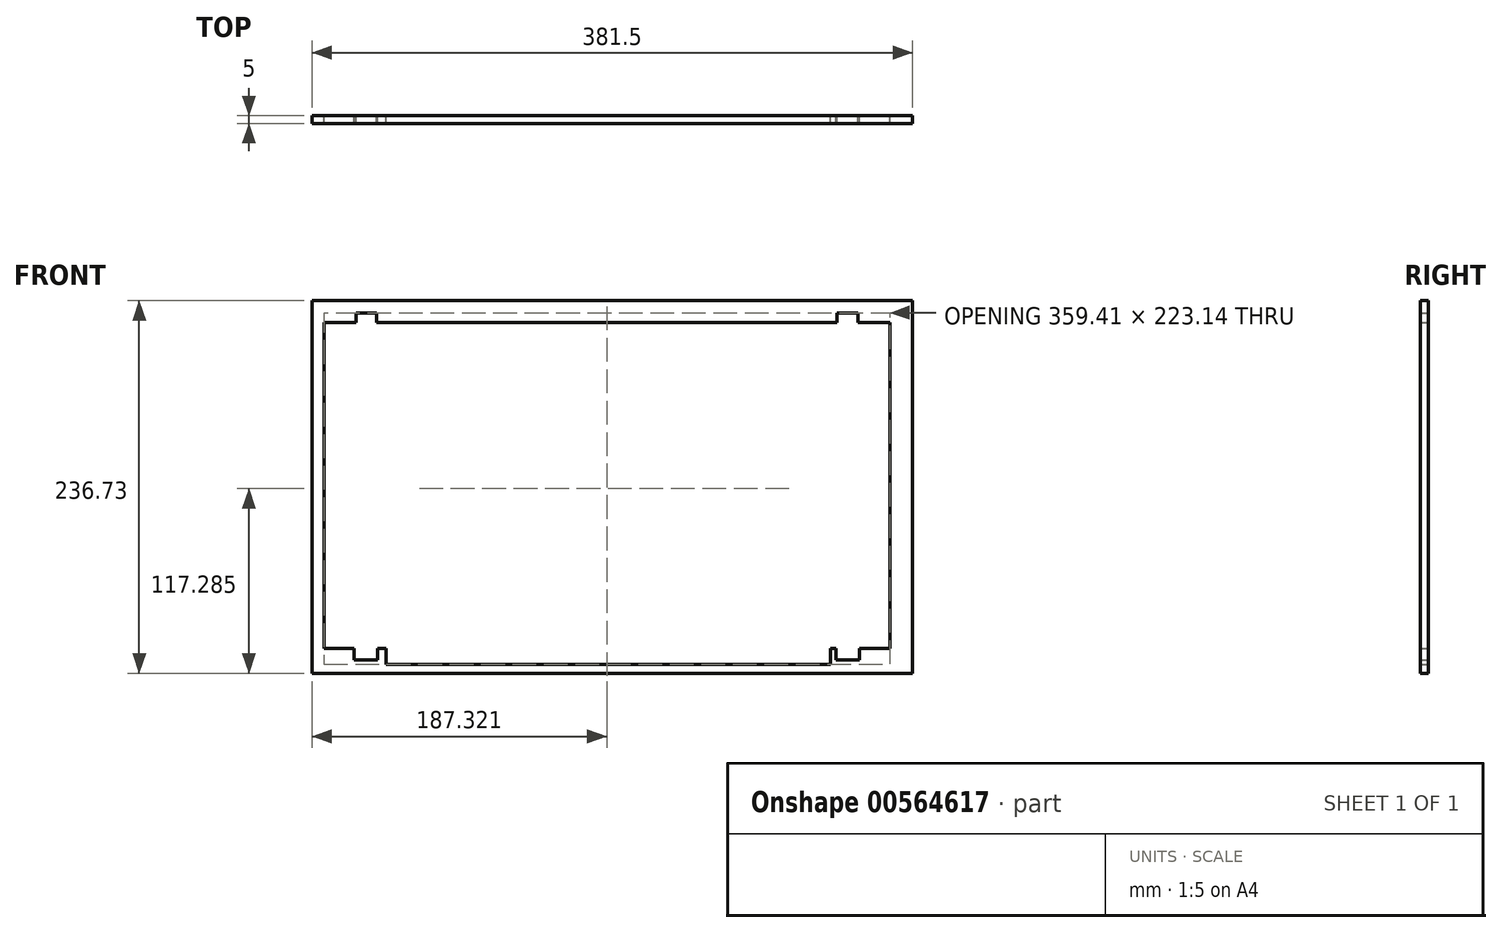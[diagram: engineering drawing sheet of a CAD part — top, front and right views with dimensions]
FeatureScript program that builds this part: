
annotation { "Feature Type Name" : "Feature", "Feature Type Description" : "" }
export const myFeature = defineFeature(function(context is Context, id is Id, definition is map)
    precondition{}
    {
        {
            var Q0;
            Q0=qCreatedBy(makeId("Front.planeOp"),FACE);
            var sketch = newSketch(context, id + "F0", { "sketchPlane" : qUnion([Q0])});
            skLineSegment(sketch, "E0.bottom", {"start": v(-180.8, 26.26) * mm, "end": v(-160.47, 26.26) * mm});
            skLineSegment(sketch, "E0.left", {"start": v(-180.8, 26.26) * mm, "end": v(-180.8, -180.75) * mm});
            skLineSegment(sketch, "E0.right", {"start": v(178.62, 26.26) * mm, "end": v(178.62, -180.75) * mm});
            skLineSegment(sketch, "E1", {"start": v(178.62, 26.26) * mm, "end": v(178.62, 32.36) * mm, "construction": true});
            skLineSegment(sketch, "E2", {"start": v(178.62, 32.36) * mm, "end": v(158.3, 32.36) * mm, "construction": true});
            skLineSegment(sketch, "E3", {"start": v(158.3, 32.36) * mm, "end": v(158.3, 26.26) * mm});
            skLineSegment(sketch, "E4", {"start": v(158.3, 32.36) * mm, "end": v(145.09, 32.36) * mm});
            skLineSegment(sketch, "E5", {"start": v(145.09, 32.36) * mm, "end": v(145.09, 26.26) * mm});
            skLineSegment(sketch, "E6", {"start": v(178.62, -180.75) * mm, "end": v(178.62, -187.99) * mm, "construction": true});
            skLineSegment(sketch, "E7", {"start": v(178.62, -187.99) * mm, "end": v(159.52, -187.99) * mm, "construction": true});
            skLineSegment(sketch, "E8", {"start": v(159.52, -187.99) * mm, "end": v(159.52, -180.75) * mm});
            skLineSegment(sketch, "E9", {"start": v(159.52, -187.99) * mm, "end": v(144.4, -187.99) * mm});
            skLineSegment(sketch, "E10", {"start": v(144.4, -187.99) * mm, "end": v(144.4, -180.75) * mm});
            skLineSegment(sketch, "E11", {"start": v(144.4, -187.99) * mm, "end": v(141.08, -187.99) * mm, "construction": true});
            skLineSegment(sketch, "E12", {"start": v(141.08, -180.75) * mm, "end": v(141.08, -190.79) * mm});
            skLineSegment(sketch, "E13", {"start": v(-1.09, 26.26) * mm, "end": v(-1.09, -180.75) * mm, "construction": true});
            skLineSegment(sketch, "E14.MirrorCS", {"start": v(-161.7, -187.99) * mm, "end": v(-146.58, -187.99) * mm});
            skLineSegment(sketch, "E15.MirrorCS", {"start": v(-180.8, -180.75) * mm, "end": v(-180.8, -187.99) * mm, "construction": true});
            skLineSegment(sketch, "E16.MirrorCS", {"start": v(-146.58, -187.99) * mm, "end": v(-141.25, -187.99) * mm, "construction": true});
            skLineSegment(sketch, "E17.MirrorCS", {"start": v(-161.7, -187.99) * mm, "end": v(-161.7, -180.75) * mm});
            skLineSegment(sketch, "E18.MirrorCS", {"start": v(-146.58, -187.99) * mm, "end": v(-146.58, -180.75) * mm});
            skLineSegment(sketch, "E19.MirrorCS", {"start": v(-180.8, -187.99) * mm, "end": v(-161.7, -187.99) * mm, "construction": true});
            skLineSegment(sketch, "E20.MirrorCS", {"start": v(178.62, -180.75) * mm, "end": v(159.52, -180.75) * mm});
            skLineSegment(sketch, "E21.MirrorCS", {"start": v(-180.8, 26.26) * mm, "end": v(-180.8, 32.36) * mm, "construction": true});
            skLineSegment(sketch, "E22.MirrorCS", {"start": v(-147.27, 32.36) * mm, "end": v(-147.27, 26.26) * mm});
            skLineSegment(sketch, "E23.MirrorCS", {"start": v(-160.47, 32.36) * mm, "end": v(-160.47, 26.26) * mm});
            skLineSegment(sketch, "E24.MirrorCS", {"start": v(-160.47, 32.36) * mm, "end": v(-147.27, 32.36) * mm});
            skLineSegment(sketch, "E25.MirrorCS", {"start": v(-180.8, 32.36) * mm, "end": v(-160.47, 32.36) * mm, "construction": true});
            skLineSegment(sketch, "E26", {"start": v(-141.25, -190.79) * mm, "end": v(-141.25, -180.75) * mm});
            skLineSegment(sketch, "E27", {"start": v(-141.25, -190.79) * mm, "end": v(141.08, -190.79) * mm});
            skLineSegment(sketch, "E28", {"start": v(-180.8, -77.24) * mm, "end": v(-188.41, -77.24) * mm, "construction": true});
            skLineSegment(sketch, "E29", {"start": v(-1.09, -180.75) * mm, "end": v(-1.09, -196.5) * mm, "construction": true});
            skLineSegment(sketch, "E30", {"start": v(-1.09, 26.26) * mm, "end": v(-1.09, 40.23) * mm, "construction": true});
            skLineSegment(sketch, "E31", {"start": v(178.62, -77.24) * mm, "end": v(193.1, -77.24) * mm, "construction": true});
            skLineSegment(sketch, "E32", {"start": v(193.1, 40.23) * mm, "end": v(193.1, -196.5) * mm});
            skLineSegment(sketch, "E33", {"start": v(193.1, -196.5) * mm, "end": v(-188.41, -196.5) * mm});
            skLineSegment(sketch, "E34", {"start": v(-188.41, -196.5) * mm, "end": v(-188.41, 40.23) * mm});
            skLineSegment(sketch, "E35", {"start": v(-188.41, 40.23) * mm, "end": v(193.1, 40.23) * mm});
            skLineSegment(sketch, "E36", {"start": v(-147.27, 26.26) * mm, "end": v(145.09, 26.26) * mm});
            skLineSegment(sketch, "E37", {"start": v(-161.7, -180.75) * mm, "end": v(-161.7, -180.75) * mm});
            skLineSegment(sketch, "E38", {"start": v(-146.58, -180.75) * mm, "end": v(-146.58, -180.75) * mm});
            skLineSegment(sketch, "E39", {"start": v(-161.7, -180.75) * mm, "end": v(-180.8, -180.75) * mm});
            skLineSegment(sketch, "E40", {"start": v(-146.58, -180.75) * mm, "end": v(144.4, -180.75) * mm});
            skLineSegment(sketch, "E41", {"start": v(144.4, -180.75) * mm, "end": v(144.4, -180.75) * mm});
            skLineSegment(sketch, "E42", {"start": v(159.52, -180.75) * mm, "end": v(159.52, -180.75) * mm});
            skLineSegment(sketch, "E43", {"start": v(159.52, -180.75) * mm, "end": v(178.62, -180.75) * mm});
            skLineSegment(sketch, "E44", {"start": v(144.4, -180.75) * mm, "end": v(-146.58, -180.75) * mm});
            skLineSegment(sketch, "E45", {"start": v(158.3, 26.26) * mm, "end": v(178.62, 26.26) * mm});
            skSolve(sketch);
        }
        {
            var Q0;
            Q0 = qSketchRegion(id + "F0", true);
            extrude(context, id + "F1", {"entities" : qUnion([Q0]), "depth" : 5 * mm, "offsetDistance" : 25 * mm});
        }
    });
